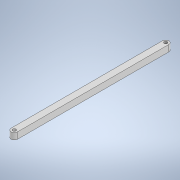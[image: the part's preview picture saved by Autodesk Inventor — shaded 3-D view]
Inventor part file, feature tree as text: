
AUTODESK INVENTOR PART (.ipt)
format: ipt  version: 2020 (Build 240168000, 168)  size: 100,352 bytes
history: native  units: mm
features: extrude x1, sketch x1
ambient origin geometry x8: Origin, YZ Plane, XZ Plane, XY Plane, X Axis, Y Axis, Z Axis, Center Point
bodies: Solid1 (feature_tree)
feature tree (2):
  extrude  "Extrusion1"  Depth=1.0mm
  sketch  "Sketch1"  dims[d0=2.0mm d1=1.0mm d2=47.25mm d3=2.0mm d4=0.0mm]
